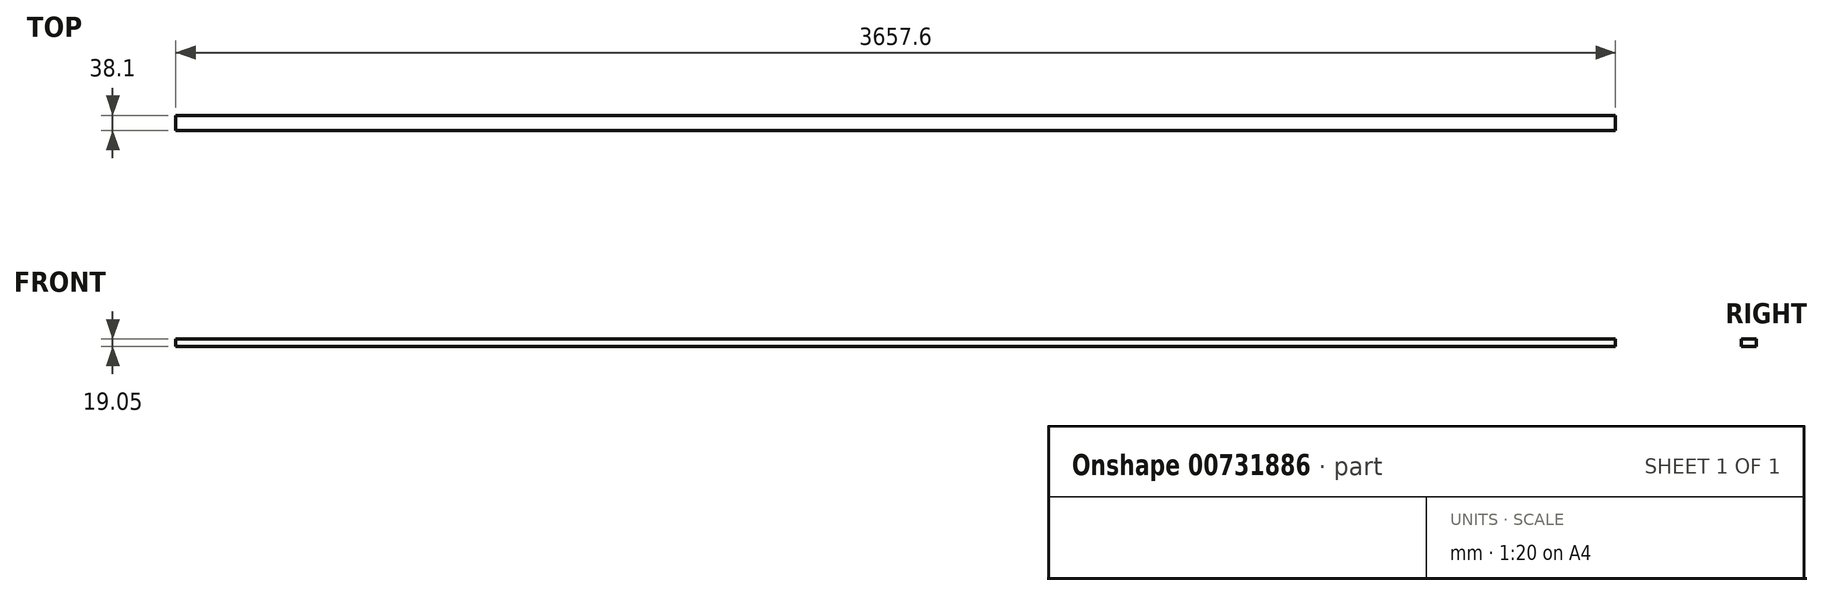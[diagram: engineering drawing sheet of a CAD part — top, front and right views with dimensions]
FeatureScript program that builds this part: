
annotation { "Feature Type Name" : "Feature", "Feature Type Description" : "" }
export const myFeature = defineFeature(function(context is Context, id is Id, definition is map)
    precondition{}
    {
        {
            var Q0;
            Q0=qCreatedBy(makeId("Right.planeOp"),FACE);
            var sketch = newSketch(context, id + "F0", { "sketchPlane" : qUnion([Q0])});
            skLineSegment(sketch, "E0.bottom", {"start": v(0, 0) * mm, "end": v(38.1, 0) * mm});
            skLineSegment(sketch, "E0.top", {"start": v(0, 19.05) * mm, "end": v(38.1, 19.05) * mm});
            skLineSegment(sketch, "E0.left", {"start": v(0, 0) * mm, "end": v(0, 19.05) * mm});
            skLineSegment(sketch, "E0.right", {"start": v(38.1, 0) * mm, "end": v(38.1, 19.05) * mm});
            skSolve(sketch);
        }
        {
            var Q0;
            Q0=makeQuery(id+"F0.imprint","IMPRINT",FACE,{"disambiguationData":[TD([[makeQuery(id+"F0.imprint","IMPRINT",EDGE,{"derivedFrom":sQuery(id+"F0.wireOp",EDGE,"E0.bottom")}),1.0]])]});
            extrude(context, id + "F1", {"entities" : qUnion([Q0]), "depth" : 3657.6 * mm, "offsetDistance" : 25.4 * mm});
        }
    });
